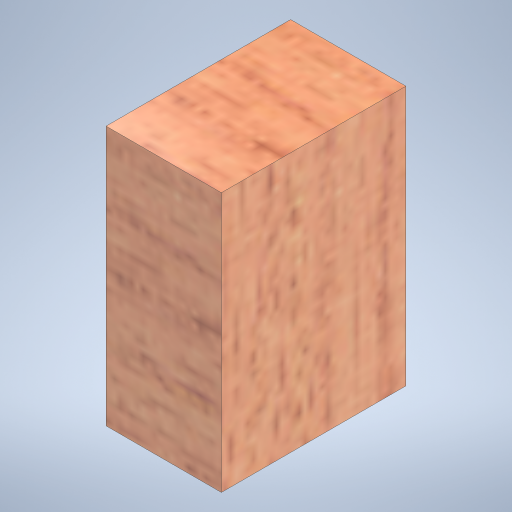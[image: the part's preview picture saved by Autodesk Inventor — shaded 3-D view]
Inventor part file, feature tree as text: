
AUTODESK INVENTOR PART (.ipt)
format: ipt  version: 2023 (Build 270158000, 158)  size: 376,832 bytes
history: native  units: mm
features: extrude x1, sketch x1
ambient origin geometry x8: Origin, YZ Plane, XZ Plane, XY Plane, X Axis, Y Axis, Z Axis, Center Point
bodies: Volumenkörper1 (feature_tree)
feature tree (2):
  extrude  "Extrusion1"  Depth=32.0mm
  sketch  "Skizze1"  dims[d0=45.0mm d1=32.0mm d2=20.0mm d3=0.0mm]
